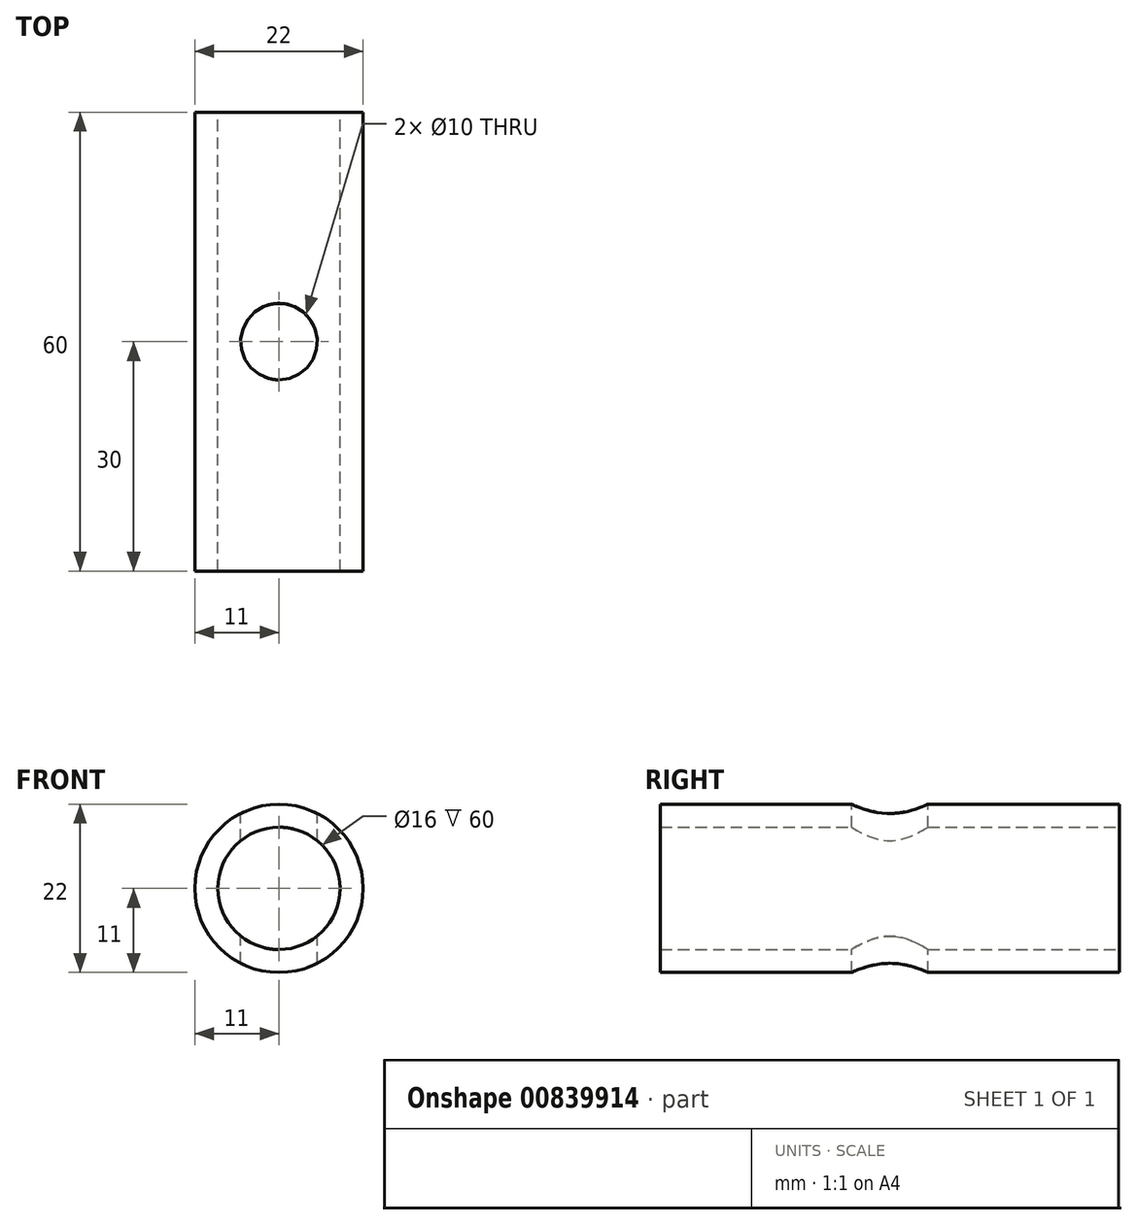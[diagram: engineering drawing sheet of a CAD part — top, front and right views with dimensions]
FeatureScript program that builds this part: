
annotation { "Feature Type Name" : "Feature", "Feature Type Description" : "" }
export const myFeature = defineFeature(function(context is Context, id is Id, definition is map)
    precondition{}
    {
        {
            var Q0;
            Q0=qCreatedBy(makeId("Front.planeOp"),FACE);
            var sketch = newSketch(context, id + "F0", { "sketchPlane" : qUnion([Q0])});
            skCircle(sketch, "E0", {"center": v(0, 0) * mm, "radius": 11 * mm});
            skCircle(sketch, "E1", {"center": v(0, 0) * mm, "radius": 8 * mm});
            skSolve(sketch);
        }
        {
            var Q0;
            Q0=makeQuery(id+"F0.imprint","IMPRINT",FACE,{"disambiguationData":[TD([[makeQuery(id+"F0.imprint","IMPRINT",EDGE,{"derivedFrom":sQuery(id+"F0.wireOp",EDGE,"E0")}),1.0]])]});
            extrude(context, id + "F1", {"entities" : qUnion([Q0]), "flatOperationType" : FlatOperationType.REMOVE, "depth" : 60 * mm, "offsetDistance" : 25 * mm, "domain" : OperationDomain.MODEL, "symmetric" : true});
        }
        {
            var Q0;
            Q0=qCreatedBy(makeId("Top.planeOp"),FACE);
            cPlane(context, id + "F2", {"entities" : qUnion([Q0]), "cplaneType" : CPlaneType.OFFSET, "offset" : 20 * mm, "width" : 150 * mm, "height" : 150 * mm});
        }
        {
            var Q0;
            Q0=qCreatedBy(id+"F2.planeOp",FACE);
            var sketch = newSketch(context, id + "F3", { "sketchPlane" : qUnion([Q0])});
            skCircle(sketch, "E2", {"center": v(0, 0) * mm, "radius": 5 * mm});
            skSolve(sketch);
        }
        {
            var Q0;
            Q0=makeQuery(id+"F3.imprint","IMPRINT",FACE,{"disambiguationData":[TD([[makeQuery(id+"F3.imprint","IMPRINT",EDGE,{"derivedFrom":sQuery(id+"F3.wireOp",EDGE,"E2")}),1.0]])]});
            extrude(context, id + "F4", {"entities" : qUnion([Q0]), "operationType" : NewBodyOperationType.REMOVE, "oppositeDirection" : true, "depth" : 40 * mm, "offsetDistance" : 25 * mm});
        }
    });
